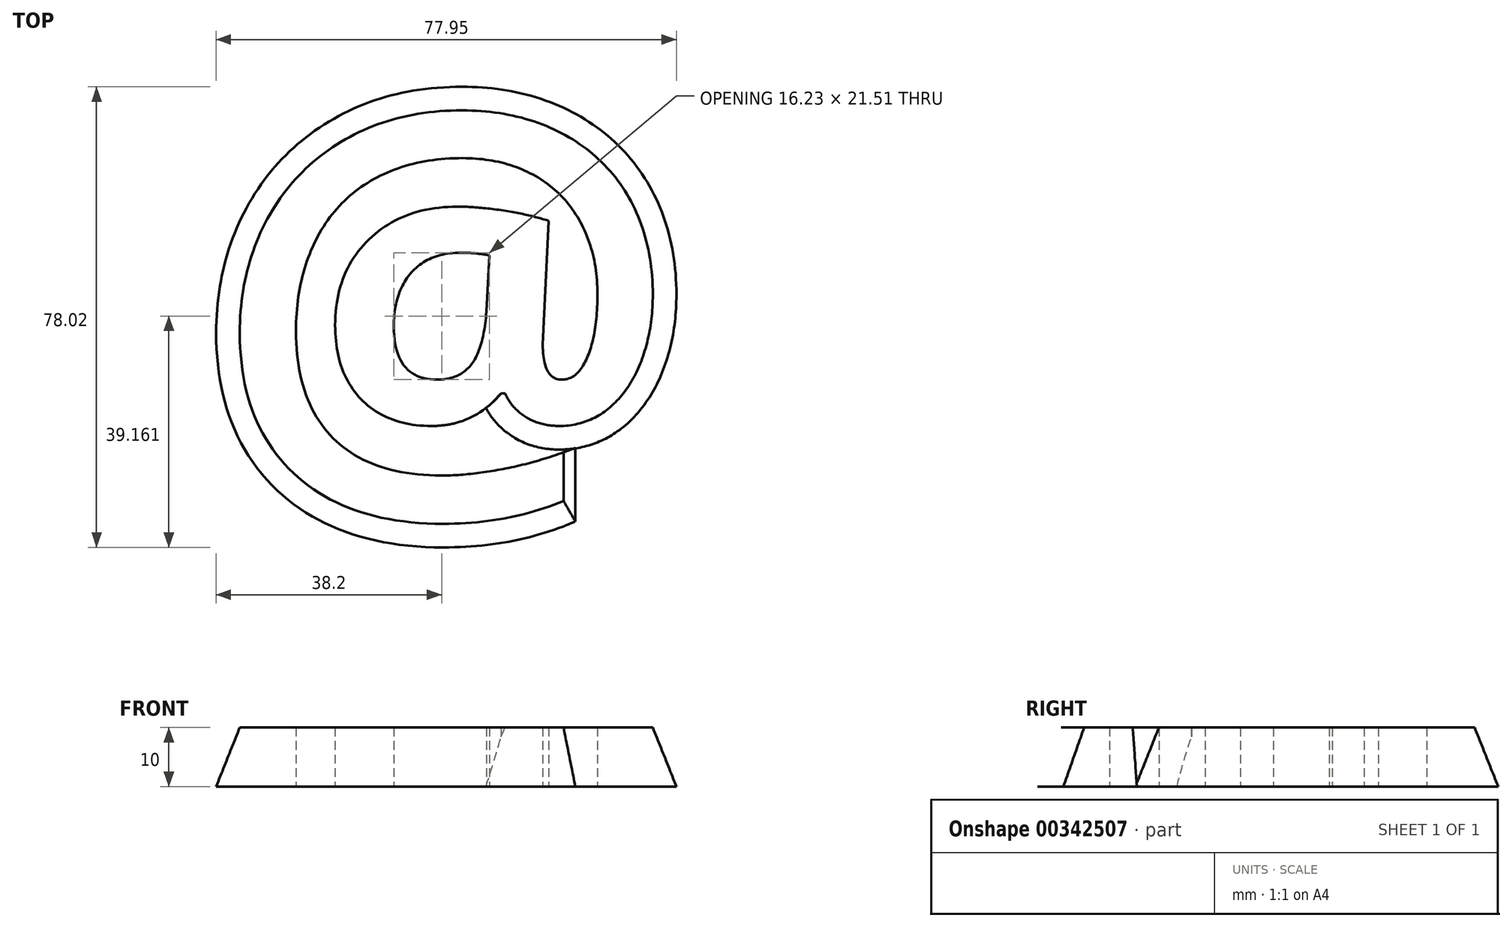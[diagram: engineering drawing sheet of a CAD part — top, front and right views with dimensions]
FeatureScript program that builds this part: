
annotation { "Feature Type Name" : "Feature", "Feature Type Description" : "" }
export const myFeature = defineFeature(function(context is Context, id is Id, definition is map)
    precondition{}
    {
        {
            var Q0;
            Q0=qCreatedBy(makeId("Top.planeOp"),FACE);
            var sketch = newSketch(context, id + "F0", { "sketchPlane" : qUnion([Q0])});
            skText(sketch, "E0", { "text": "@", "fontName": "OpenSans-Bold.ttf"});
            const initialGuessF0  = {"E0": [-0.02836, -0.03784, 1, 0, 0.06316]};
            skSetInitialGuess(sketch, initialGuessF0);
            skSolve(sketch);
        }
        {
            var Q0;
            Q0 = qSketchRegion(id + "F0", true);
            extrude(context, id + "F1", {"entities" : qUnion([Q0]), "depth" : 10 * mm});
        }
        {
            var Q0;
            Q0=makeQuery(id+"F1.opExtrude","CAP_FACE",FACE,{"disambiguationData":[OSD([sQuery(id+"F0.wireOp",EDGE,"E0.sketch_text.stroke-0"),sQuery(id+"F0.wireOp",EDGE,"E0.sketch_text.stroke-1"),sQuery(id+"F0.wireOp",EDGE,"E0.sketch_text.stroke-2"),sQuery(id+"F0.wireOp",EDGE,"E0.sketch_text.stroke-3"),sQuery(id+"F0.wireOp",EDGE,"E0.sketch_text.stroke-4"),sQuery(id+"F0.wireOp",EDGE,"E0.sketch_text.stroke-5"),sQuery(id+"F0.wireOp",EDGE,"E0.sketch_text.stroke-6"),sQuery(id+"F0.wireOp",EDGE,"E0.sketch_text.stroke-7"),sQuery(id+"F0.wireOp",EDGE,"E0.sketch_text.stroke-8"),sQuery(id+"F0.wireOp",EDGE,"E0.sketch_text.stroke-9"),sQuery(id+"F0.wireOp",EDGE,"E0.sketch_text.stroke-10"),sQuery(id+"F0.wireOp",EDGE,"E0.sketch_text.stroke-11"),sQuery(id+"F0.wireOp",EDGE,"E0.sketch_text.stroke-12"),sQuery(id+"F0.wireOp",EDGE,"E0.sketch_text.stroke-13"),sQuery(id+"F0.wireOp",EDGE,"E0.sketch_text.stroke-14"),sQuery(id+"F0.wireOp",EDGE,"E0.sketch_text.stroke-15"),sQuery(id+"F0.wireOp",EDGE,"E0.sketch_text.stroke-16"),sQuery(id+"F0.wireOp",EDGE,"E0.sketch_text.stroke-17"),sQuery(id+"F0.wireOp",EDGE,"E0.sketch_text.stroke-18"),sQuery(id+"F0.wireOp",EDGE,"E0.sketch_text.stroke-19"),sQuery(id+"F0.wireOp",EDGE,"E0.sketch_text.stroke-20"),sQuery(id+"F0.wireOp",EDGE,"E0.sketch_text.stroke-21"),sQuery(id+"F0.wireOp",EDGE,"E0.sketch_text.stroke-22"),sQuery(id+"F0.wireOp",EDGE,"E0.sketch_text.stroke-23"),sQuery(id+"F0.wireOp",EDGE,"E0.sketch_text.stroke-24"),sQuery(id+"F0.wireOp",EDGE,"E0.sketch_text.stroke-25"),sQuery(id+"F0.wireOp",EDGE,"E0.sketch_text.stroke-26"),sQuery(id+"F0.wireOp",EDGE,"E0.sketch_text.stroke-27"),sQuery(id+"F0.wireOp",EDGE,"E0.sketch_text.stroke-28"),sQuery(id+"F0.wireOp",EDGE,"E0.sketch_text.stroke-29"),sQuery(id+"F0.wireOp",EDGE,"E0.sketch_text.stroke-30"),sQuery(id+"F0.wireOp",EDGE,"E0.sketch_text.stroke-31"),sQuery(id+"F0.wireOp",EDGE,"E0.sketch_text.stroke-32"),sQuery(id+"F0.wireOp",EDGE,"E0.sketch_text.stroke-33"),sQuery(id+"F0.wireOp",EDGE,"E0.sketch_text.stroke-34"),sQuery(id+"F0.wireOp",EDGE,"E0.sketch_text.stroke-35"),sQuery(id+"F0.wireOp",EDGE,"E0.sketch_text.stroke-36"),sQuery(id+"F0.wireOp",EDGE,"E0.sketch_text.stroke-37"),sQuery(id+"F0.wireOp",EDGE,"E0.sketch_text.stroke-38"),sQuery(id+"F0.wireOp",EDGE,"E0.sketch_text.stroke-39"),sQuery(id+"F0.wireOp",EDGE,"E0.sketch_text.stroke-40"),sQuery(id+"F0.wireOp",EDGE,"E0.sketch_text.stroke-41"),sQuery(id+"F0.wireOp",EDGE,"E0.sketch_text.stroke-42"),sQuery(id+"F0.wireOp",EDGE,"E0.sketch_text.stroke-43")])],"isStart":true});
            var sketch = newSketch(context, id + "F2", { "sketchPlane" : qUnion([Q0])});
            skCircle(sketch, "E1", {"center": v(9.46, 9.48) * mm, "radius": 64.5 * mm});
            skSolve(sketch);
        }
        {
            var Q0;
            Q0 = qSketchRegion(id + "F2", true);
            extrude(context, id + "F3", {"entities" : qUnion([Q0]), "operationType" : NewBodyOperationType.ADD, "depth" : 25 * mm});
        }
        {
            var Q0;
            Q0=makeQuery(id+"F1.opExtrude","CAP_EDGE",EDGE,{"disambiguationData":[OSD([sQuery(id+"F0.wireOp",EDGE,"E0.sketch_text.stroke-28")])],"isStart":true});
            chamfer(context, id + "F4", {"entities" : qUnion([Q0]), "chamferType" : ChamferType.TWO_OFFSETS, "width1" : 4 * mm, "oppositeDirection" : false, "width2" : 10 * mm, "tangentPropagation" : true});
        }
        {
            var Q0;
            Q0=makeQuery(id+"F1.opExtrude","CAP_EDGE",EDGE,{"disambiguationData":[OSD([sQuery(id+"F0.wireOp",EDGE,"E0.sketch_text.stroke-27")])],"isStart":true});
            var Q1;
            Q1=makeQuery(id+"F1.opExtrude","CAP_EDGE",EDGE,{"disambiguationData":[OSD([sQuery(id+"F0.wireOp",EDGE,"E0.sketch_text.stroke-43")])],"isStart":true});
            chamfer(context, id + "F5", {"entities" : qUnion([Q0, Q1]), "chamferType" : ChamferType.TWO_OFFSETS, "width1" : 2 * mm, "oppositeDirection" : false, "width2" : 10 * mm, "tangentPropagation" : true});
        }
        {
            var Q0;
            {var subQ0=sQuery(id+"F2.wireOp",EDGE,"E1");Q0=makeQuery(id+"F5.opChamfer","SPLIT",FACE,{"disambiguationData":[OD(0.0)],"derivedFrom":makeQuery(id+"F3.boolean.opBoolean","SPLIT",FACE,{"disambiguationData":[TD([makeQuery(id+"F1.opExtrude","SWEPT_FACE",FACE,{"disambiguationData":[OSD([sQuery(id+"F0.wireOp",EDGE,"E0.sketch_text.stroke-0")])]})])],"derivedFrom":makeQuery(id+"F3.opExtrude","CAP_FACE",FACE,{"disambiguationData":[OSD([subQ0])],"isStart":true})})});}
            var sketch = newSketch(context, id + "F6", { "sketchPlane" : qUnion([Q0])});
            skCircle(sketch, "E2", {"center": v(0, 0) * mm, "radius": 83.63 * mm});
            skSolve(sketch);
        }
        {
            var Q0;
            Q0 = qSketchRegion(id + "F6", true);
            extrude(context, id + "F7", {"entities" : qUnion([Q0]), "operationType" : NewBodyOperationType.REMOVE, "oppositeDirection" : true, "depth" : 36.6 * mm});
        }
    });
